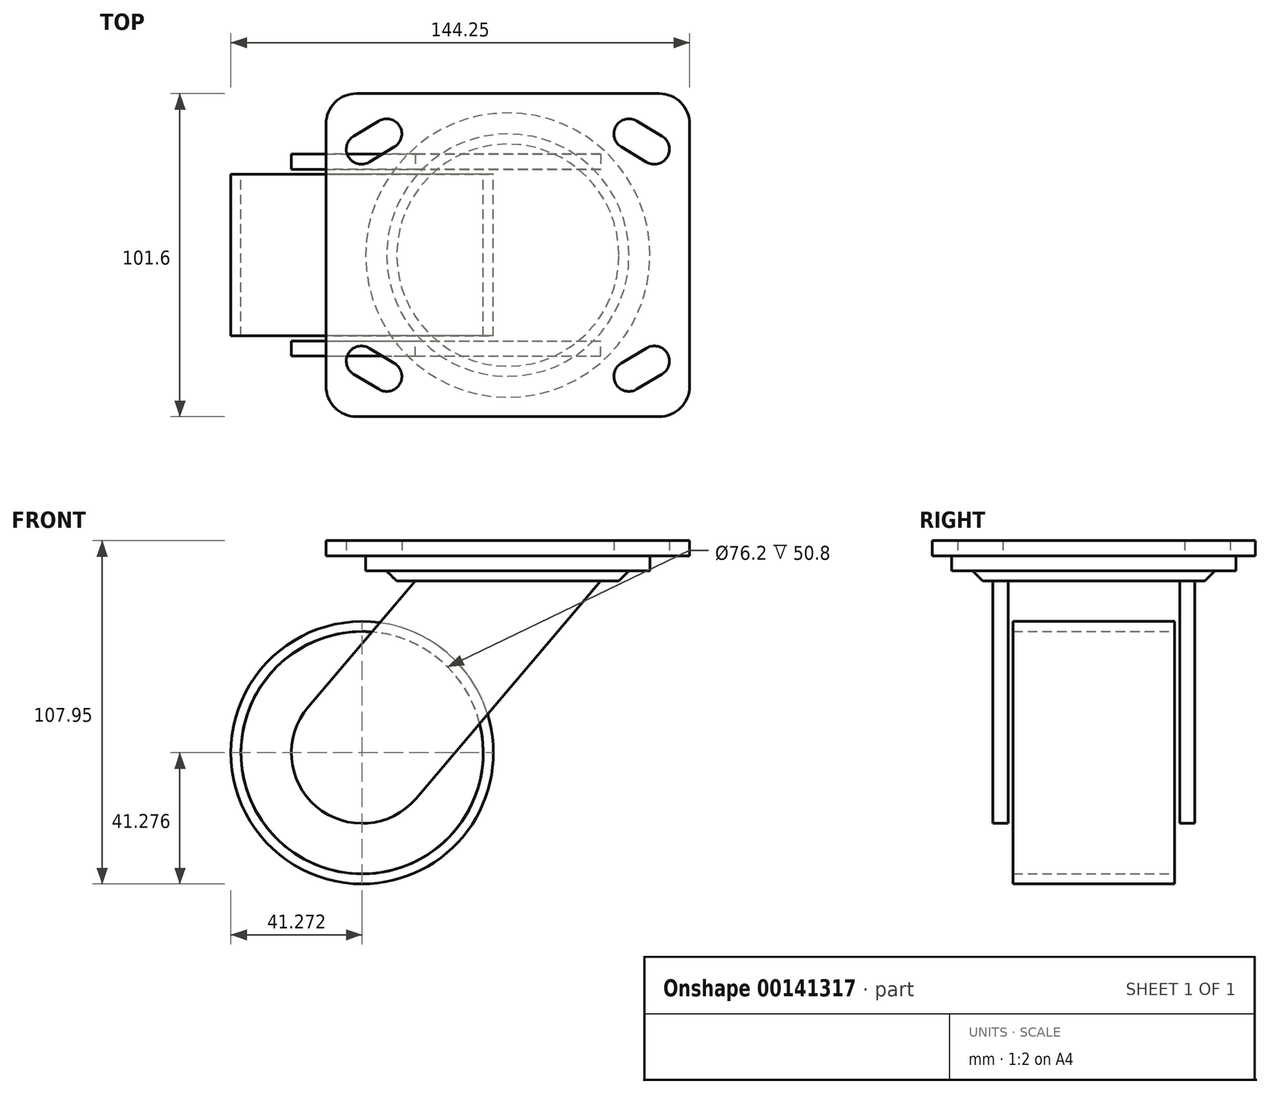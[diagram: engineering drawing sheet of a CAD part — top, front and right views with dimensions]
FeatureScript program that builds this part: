
annotation { "Feature Type Name" : "Feature", "Feature Type Description" : "" }
export const myFeature = defineFeature(function(context is Context, id is Id, definition is map)
    precondition{}
    {
        {
            var Q0;
            Q0=qCreatedBy(makeId("Top.planeOp"),FACE);
            var sketch = newSketch(context, id + "F0", { "sketchPlane" : qUnion([Q0])});
            skLineSegment(sketch, "E0.bottom", {"start": v(47.62, 50.8) * mm, "end": v(-47.63, 50.8) * mm});
            skLineSegment(sketch, "E0.top", {"start": v(47.63, -50.8) * mm, "end": v(-47.62, -50.8) * mm});
            skLineSegment(sketch, "E0.left", {"start": v(57.15, 41.28) * mm, "end": v(57.15, -41.27) * mm});
            skLineSegment(sketch, "E0.right", {"start": v(-57.15, 41.27) * mm, "end": v(-57.15, -41.28) * mm});
            skPoint(sketch, "E0.middle", {"position": v(0, 0) * mm});
            skPoint(sketch, "E1.visualSharp", {"position": v(-57.15, -50.8) * mm});
            skArc(sketch, "E1.filletArc", {"start": v(-57.15, -41.28) * mm, "mid": v(-54.36, -48.01) * mm, "end": v(-47.62, -50.8) * mm});
            skPoint(sketch, "E2.visualSharp", {"position": v(57.15, -50.8) * mm});
            skArc(sketch, "E2.filletArc", {"start": v(47.63, -50.8) * mm, "mid": v(54.36, -48.01) * mm, "end": v(57.15, -41.27) * mm});
            skPoint(sketch, "E3.visualSharp", {"position": v(57.15, 50.8) * mm});
            skArc(sketch, "E3.filletArc", {"start": v(57.15, 41.28) * mm, "mid": v(54.36, 48.01) * mm, "end": v(47.62, 50.8) * mm});
            skPoint(sketch, "E4.visualSharp", {"position": v(-57.15, 50.8) * mm});
            skArc(sketch, "E4.filletArc", {"start": v(-47.63, 50.8) * mm, "mid": v(-54.36, 48.01) * mm, "end": v(-57.15, 41.27) * mm});
            skSolve(sketch);
        }
        {
            var Q0;
            Q0 = qSketchRegion(id + "F0", true);
            extrude(context, id + "F1", {"entities" : qUnion([Q0]), "endBound" : BoundingType.SYMMETRIC, "depth" : 4.76 * mm});
        }
        {
            var Q0;
            Q0=makeQuery(id+"F1.opExtrude","CAP_FACE",FACE,{"disambiguationData":[OSD([sQuery(id+"F0.wireOp",EDGE,"E0.bottom"),sQuery(id+"F0.wireOp",EDGE,"E0.top"),sQuery(id+"F0.wireOp",EDGE,"E0.left"),sQuery(id+"F0.wireOp",EDGE,"E0.right")])],"isStart":true});
            var sketch = newSketch(context, id + "F2", { "sketchPlane" : qUnion([Q0])});
            skPoint(sketch, "E5.startSnap0", {"position": v(0, 50.8) * mm});
            skPoint(sketch, "E6.endSnap0", {"position": v(57.15, 0) * mm});
            skArc(sketch, "E7", {"start": v(-48.49, 37.42) * mm, "mid": v(-50.12, 30.89) * mm, "end": v(-43.59, 29.25) * mm});
            skArc(sketch, "E8", {"start": v(43.59, 29.25) * mm, "mid": v(50.12, 30.89) * mm, "end": v(48.49, 37.42) * mm});
            skArc(sketch, "E9", {"start": v(-40.55, -42.18) * mm, "mid": v(-34.02, -40.55) * mm, "end": v(-35.65, -34.02) * mm});
            skArc(sketch, "E10", {"start": v(48.49, -37.42) * mm, "mid": v(50.12, -30.89) * mm, "end": v(43.59, -29.25) * mm});
            skLineSegment(sketch, "E11.0", {"start": v(-40.55, 42.18) * mm, "end": v(-48.49, 37.42) * mm});
            skLineSegment(sketch, "E12.0", {"start": v(-35.65, 34.02) * mm, "end": v(-43.59, 29.25) * mm});
            skLineSegment(sketch, "E13.0", {"start": v(35.65, 34.02) * mm, "end": v(43.59, 29.25) * mm});
            skLineSegment(sketch, "E14.0", {"start": v(40.55, 42.18) * mm, "end": v(48.49, 37.42) * mm});
            skLineSegment(sketch, "E15.0", {"start": v(-48.49, -37.42) * mm, "end": v(-40.55, -42.18) * mm});
            skLineSegment(sketch, "E16.0", {"start": v(-43.59, -29.25) * mm, "end": v(-35.65, -34.02) * mm});
            skLineSegment(sketch, "E17.0", {"start": v(40.55, -42.18) * mm, "end": v(48.49, -37.42) * mm});
            skLineSegment(sketch, "E18.0", {"start": v(35.65, -34.02) * mm, "end": v(43.59, -29.25) * mm});
            skArc(sketch, "E19.trimOffspring", {"start": v(-43.59, -29.25) * mm, "mid": v(-50.12, -30.89) * mm, "end": v(-48.49, -37.42) * mm});
            skArc(sketch, "E20.trimOffspring", {"start": v(35.65, -34.02) * mm, "mid": v(34.02, -40.55) * mm, "end": v(40.55, -42.18) * mm});
            skArc(sketch, "E21.trimOffspring", {"start": v(40.55, 42.18) * mm, "mid": v(34.02, 40.55) * mm, "end": v(35.65, 34.02) * mm});
            skArc(sketch, "E22.trimOffspring", {"start": v(-35.65, 34.02) * mm, "mid": v(-34.02, 40.55) * mm, "end": v(-40.55, 42.18) * mm});
            skSolve(sketch);
        }
        {
            var Q0;
            Q0 = qSketchRegion(id + "F2", true);
            extrude(context, id + "F3", {"entities" : qUnion([Q0]), "operationType" : NewBodyOperationType.REMOVE, "oppositeDirection" : true, "depth" : 25.4 * mm});
        }
        {
            var Q0;
            Q0=makeQuery(id+"F1.opExtrude","CAP_FACE",FACE,{"disambiguationData":[OSD([sQuery(id+"F0.wireOp",EDGE,"E0.bottom"),sQuery(id+"F0.wireOp",EDGE,"E0.top"),sQuery(id+"F0.wireOp",EDGE,"E0.left"),sQuery(id+"F0.wireOp",EDGE,"E0.right"),sQuery(id+"F0.wireOp",EDGE,"E1.filletArc"),sQuery(id+"F0.wireOp",EDGE,"E2.filletArc"),sQuery(id+"F0.wireOp",EDGE,"E3.filletArc"),sQuery(id+"F0.wireOp",EDGE,"E4.filletArc")])],"isStart":true});
            var sketch = newSketch(context, id + "F4", { "sketchPlane" : qUnion([Q0])});
            skCircle(sketch, "E23", {"center": v(0, 0) * mm, "radius": 44.7 * mm});
            skSolve(sketch);
        }
        {
            var Q0;
            Q0 = qSketchRegion(id + "F4", true);
            extrude(context, id + "F5", {"entities" : qUnion([Q0]), "operationType" : NewBodyOperationType.ADD, "depth" : 4.76 * mm});
        }
        {
            var Q0;
            Q0=makeQuery(id+"F5.opExtrude","CAP_FACE",FACE,{"disambiguationData":[OSD([sQuery(id+"F4.wireOp",EDGE,"E23")])],"isStart":false});
            var sketch = newSketch(context, id + "F6", { "sketchPlane" : qUnion([Q0])});
            skCircle(sketch, "E24", {"center": v(0, 0) * mm, "radius": 38.1 * mm});
            skSolve(sketch);
        }
        {
            var Q0;
            Q0=makeQuery(id+"F6.imprint","IMPRINT",FACE,{"disambiguationData":[TD([[makeQuery(id+"F6.imprint","IMPRINT",EDGE,{"derivedFrom":sQuery(id+"F6.wireOp",EDGE,"E24")}),1.0]])]});
            extrude(context, id + "F7", {"entities" : qUnion([Q0]), "depth" : 3.17 * mm});
        }
        {
            var Q0;
            Q0=makeQuery(id+"F7.opExtrude","CAP_FACE",FACE,{"disambiguationData":[OSD([sQuery(id+"F6.wireOp",EDGE,"E24")])],"isStart":false});
            chamfer(context, id + "F8", {"entities" : qUnion([Q0]), "width" : 3.17 * mm, "tangentPropagation" : true});
        }
        {
            var Q0;
            Q0=qCreatedBy(makeId("Front.planeOp"),FACE);
            var sketch = newSketch(context, id + "F9", { "sketchPlane" : qUnion([Q0])});
            skLineSegment(sketch, "E25", {"start": v(-187.88, -64.3) * mm, "end": v(166.1, -64.3) * mm});
            skLineSegment(sketch, "E26", {"start": v(-45.83, 51.7) * mm, "end": v(-45.83, -121.68) * mm});
            skCircle(sketch, "E27", {"center": v(-45.83, -64.3) * mm, "radius": 41.28 * mm});
            skSolve(sketch);
        }
        {
            var Q0;
            Q0 = qSketchRegion(id + "F9", true);
            extrude(context, id + "F10", {"entities" : qUnion([Q0]), "endBound" : BoundingType.SYMMETRIC, "depth" : 50.8 * mm});
        }
        {
            var Q0;
            Q0=makeQuery(id+"F10.opExtrude","CAP_FACE",FACE,{"disambiguationData":[OSD([sQuery(id+"F9.wireOp",EDGE,"E27")])],"isStart":false});
            var sketch = newSketch(context, id + "F11", { "sketchPlane" : qUnion([Q0])});
            skLineSegment(sketch, "E28", {"start": v(-29.16, -10.32) * mm, "end": v(29.16, -10.32) * mm});
            skLineSegment(sketch, "E29.0", {"start": v(-28.89, -78.68) * mm, "end": v(16.94, -24.7) * mm});
            skLineSegment(sketch, "E30.0", {"start": v(-62.77, -49.9) * mm, "end": v(-29.16, -10.32) * mm});
            skLineSegment(sketch, "E31", {"start": v(16.94, -24.7) * mm, "end": v(29.16, -10.32) * mm});
            skArc(sketch, "E32", {"start": v(-62.77, -49.9) * mm, "mid": v(-60.21, -81.24) * mm, "end": v(-28.89, -78.68) * mm});
            skSolve(sketch);
        }
        {
            var Q0;
            Q0 = qSketchRegion(id + "F11", true);
            extrude(context, id + "F12", {"entities" : qUnion([Q0]), "depth" : 6.35 * mm});
        }
        {
            var Q0;
            Q0=makeQuery(id+"F12.opExtrude","CAP_FACE",FACE,{"disambiguationData":[OSD([sQuery(id+"F11.wireOp",EDGE,"E28"),sQuery(id+"F11.wireOp",EDGE,"E29.0"),sQuery(id+"F11.wireOp",EDGE,"E30.0"),sQuery(id+"F11.wireOp",EDGE,"E31"),sQuery(id+"F11.wireOp",EDGE,"E32")])],"isStart":true});
            extrude(context, id + "F13", {"entities" : qUnion([Q0]), "operationType" : NewBodyOperationType.REMOVE, "oppositeDirection" : true, "depth" : 1.59 * mm});
        }
        {
            var Q0;
            Q0=makeQuery(id+"F10.opExtrude","CAP_FACE",FACE,{"disambiguationData":[OSD([sQuery(id+"F9.wireOp",EDGE,"E27")])],"isStart":true});
            var sketch = newSketch(context, id + "F14", { "sketchPlane" : qUnion([Q0])});
            skCircle(sketch, "E33", {"center": v(45.83, -64.3) * mm, "radius": 38.1 * mm});
            skSolve(sketch);
        }
        {
            var Q0;
            Q0=makeQuery(id+"F14.imprint","IMPRINT",FACE,{"disambiguationData":[TD([[makeQuery(id+"F14.imprint","IMPRINT",EDGE,{"derivedFrom":sQuery(id+"F14.wireOp",EDGE,"E33")}),1.0]])]});
            extrude(context, id + "F15", {"entities" : qUnion([Q0]), "operationType" : NewBodyOperationType.REMOVE, "endBound" : BoundingType.UP_TO_NEXT, "oppositeDirection" : true, "depth" : 25.4 * mm});
        }
        {
            var Q0;
            Q0=makeQuery(id+"F14.imprint","IMPRINT",FACE,{"disambiguationData":[TD([[makeQuery(id+"F14.imprint","IMPRINT",EDGE,{"derivedFrom":sQuery(id+"F14.wireOp",EDGE,"E33")}),1.0]])]});
            extrude(context, id + "F16", {"entities" : qUnion([Q0]), "oppositeDirection" : true, "depth" : 50.8 * mm});
        }
        {
            var Q0;
            Q0=makeQuery(id+"F14.imprint","IMPRINT",FACE,{"disambiguationData":[TD([[makeQuery(id+"F14.imprint","IMPRINT",EDGE,{"derivedFrom":sQuery(id+"F14.wireOp",EDGE,"E33")}),1.0]])]});
            var sketch = newSketch(context, id + "F17", { "sketchPlane" : qUnion([Q0])});
            skLineSegment(sketch, "E34", {"start": v(-29.16, -10.32) * mm, "end": v(29.16, -10.32) * mm});
            skLineSegment(sketch, "E35.0", {"start": v(62.77, -49.9) * mm, "end": v(29.16, -10.32) * mm});
            skLineSegment(sketch, "E36.0", {"start": v(28.89, -78.68) * mm, "end": v(-16.94, -24.7) * mm});
            skLineSegment(sketch, "E37", {"start": v(-16.94, -24.7) * mm, "end": v(-29.16, -10.32) * mm});
            skArc(sketch, "E38", {"start": v(28.89, -78.68) * mm, "mid": v(60.21, -81.24) * mm, "end": v(62.77, -49.9) * mm});
            skSolve(sketch);
        }
        {
            var Q0;
            {var subQ0=sQuery(id+"F17.wireOp",EDGE,"E38");Q0=makeQuery(id+"F17.imprint","IMPRINT",FACE,{"disambiguationData":[TD([[makeQuery(id+"F17.imprint","IMPRINT",EDGE,{"derivedFrom":subQ0}),1.0]])]});}
            var Q1;
            {var subQ5=sQuery(id+"F17.wireOp",EDGE,"E34");Q1=makeQuery(id+"F17.imprint","IMPRINT",FACE,{"disambiguationData":[TD([[makeQuery(id+"F17.imprint","IMPRINT",EDGE,{"derivedFrom":subQ5}),-1.0]])]});}
            extrude(context, id + "F18", {"entities" : qUnion([Q0, Q1]), "depth" : 6.35 * mm});
        }
        {
            var Q0;
            Q0=makeQuery(id+"F18.opExtrude","CAP_FACE",FACE,{"disambiguationData":[OSD([sQuery(id+"F17.wireOp",EDGE,"E34"),sQuery(id+"F17.wireOp",EDGE,"E35.0"),sQuery(id+"F17.wireOp",EDGE,"E36.0"),sQuery(id+"F17.wireOp",EDGE,"E37"),sQuery(id+"F17.wireOp",EDGE,"E38")])],"isStart":true});
            extrude(context, id + "F19", {"entities" : qUnion([Q0]), "operationType" : NewBodyOperationType.REMOVE, "oppositeDirection" : true, "depth" : 1.59 * mm});
        }
    });
